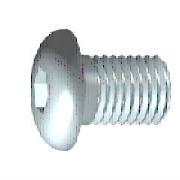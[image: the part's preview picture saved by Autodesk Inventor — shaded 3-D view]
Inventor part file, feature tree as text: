
AUTODESK INVENTOR PART (.ipt)
format: ipt  version: 2022 (Build 260153000, 153)  size: 207,872 bytes
history: native  units: mm (DEFAULTED — no unit token found)
features: sketch x2, extrude x1, plane x1, fillet x1
ambient origin geometry x7: Origin, YZ Plane, XY Plane, X Axis, Y Axis, Z Axis, Center Point
bodies: Solid1 (feature_tree), Body (feature_tree)
feature tree (5):
  extrude  "Slot"  Depth=1.65mm
  plane  "Work Plane1"
  fillet  "Fillet2"  Radius=1.65mm
  sketch  "Sketch1"  dims[d1=11.0mm d2=0.306825mm d3=1.65mm]
  sketch  "Sketch2"  dims[d4=1.04mm d5=60.0deg d6=3.0mm d7=3.0mm d8=2.309401mm d9=5.7mm d10=90.0deg d11=10.0mm d12=0.0mm d13=11.0mm d14=0.0mm d15=0.306725mm d16=0.306725mm d17=1.45mm d19=0.0mm d26=12.0mm d27=45.0deg d28=0.0mm d29=0.0mm d30=0.1mm]
